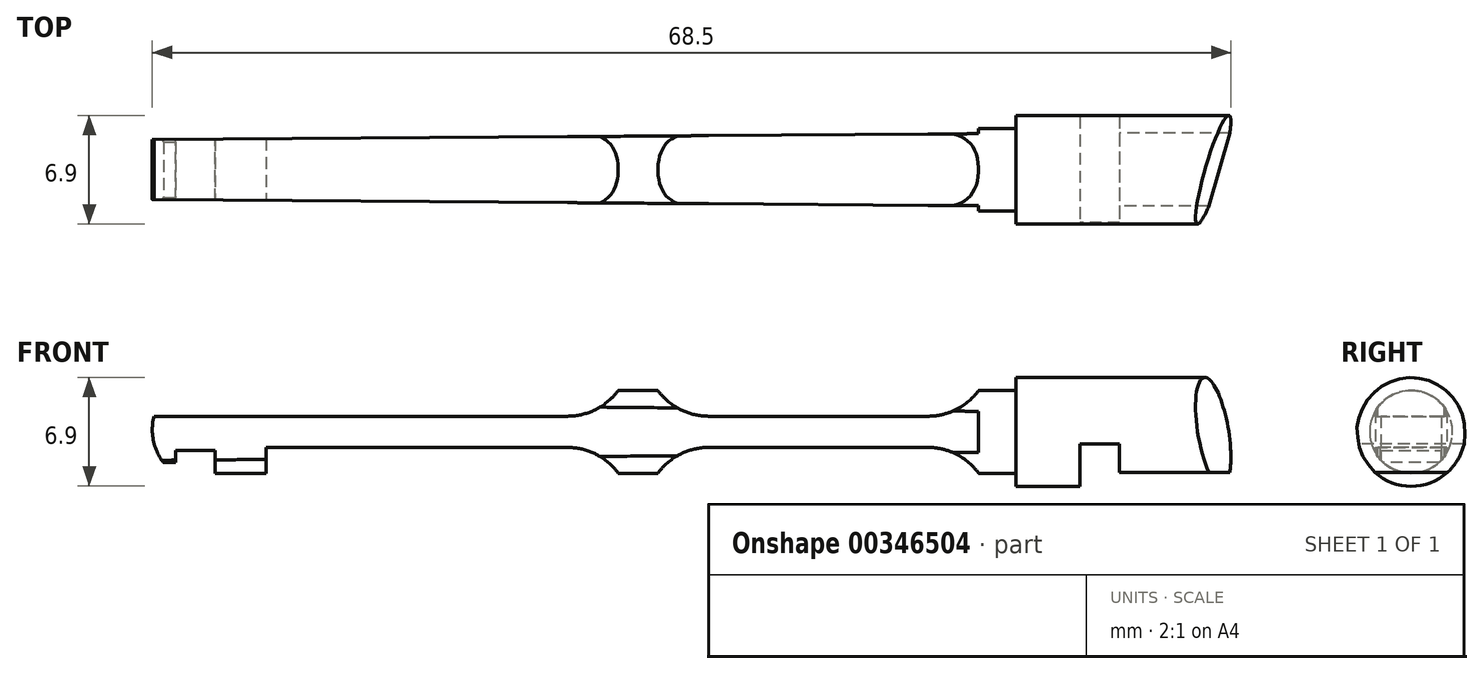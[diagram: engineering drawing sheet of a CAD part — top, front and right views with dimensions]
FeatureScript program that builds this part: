
annotation { "Feature Type Name" : "Feature", "Feature Type Description" : "" }
export const myFeature = defineFeature(function(context is Context, id is Id, definition is map)
    precondition{}
    {
        {
            var Q0;
            Q0=qCreatedBy(makeId("Right.planeOp"),FACE);
            var sketch = newSketch(context, id + "F0", { "sketchPlane" : qUnion([Q0])});
            skCircle(sketch, "E0", {"center": v(0, 0) * mm, "radius": 3.45 * mm});
            skSolve(sketch);
        }
        {
            var Q0;
            Q0 = qSketchRegion(id + "F0", true);
            extrude(context, id + "F1", {"entities" : qUnion([Q0]), "depth" : 4.06 * mm, "offsetDistance" : 25.4 * mm});
        }
        {
            var Q0;
            Q0=makeQuery(id+"F1.opExtrude","CAP_FACE",FACE,{"disambiguationData":[OSD([sQuery(id+"F0.wireOp",EDGE,"E0")])],"isStart":false});
            var sketch = newSketch(context, id + "F2", { "sketchPlane" : qUnion([Q0])});
            skCircle(sketch, "E1.0", {"center": v(0, 0) * mm, "radius": 3.45 * mm});
            skSolve(sketch);
        }
        {
            var Q0;
            Q0 = qSketchRegion(id + "F2", true);
            extrude(context, id + "F3", {"entities" : qUnion([Q0]), "operationType" : NewBodyOperationType.ADD, "depth" : 9.58 * mm, "offsetDistance" : 25.4 * mm});
        }
        {
            var Q0;
            Q0=qCreatedBy(makeId("Front.planeOp"),FACE);
            var sketch = newSketch(context, id + "F4", { "sketchPlane" : qUnion([Q0])});
            skLineSegment(sketch, "E2.bottom", {"start": v(4.06, -0.76) * mm, "end": v(6.58, -0.76) * mm});
            skLineSegment(sketch, "E2.top", {"start": v(4.06, -7.11) * mm, "end": v(6.58, -7.11) * mm});
            skLineSegment(sketch, "E2.left", {"start": v(4.06, -0.76) * mm, "end": v(4.06, -7.11) * mm});
            skLineSegment(sketch, "E2.right", {"start": v(6.58, -0.76) * mm, "end": v(6.58, -7.11) * mm});
            skLineSegment(sketch, "E3.0", {"start": v(13.64, 3.45) * mm, "end": v(13.64, -3.45) * mm, "construction": true});
            skSolve(sketch);
        }
        {
            var Q0;
            Q0 = qSketchRegion(id + "F4", true);
            extrude(context, id + "F5", {"entities" : qUnion([Q0]), "operationType" : NewBodyOperationType.REMOVE, "endBound" : BoundingType.THROUGH_ALL, "oppositeDirection" : true, "depth" : 25.4 * mm, "offsetDistance" : 25.4 * mm, "hasSecondDirection" : true, "secondDirectionBound" : BoundingType.THROUGH_ALL, "secondDirectionOppositeDirection" : false, "secondDirectionDepth" : 25.4 * mm});
        }
        {
            var Q0;
            Q0=qCreatedBy(makeId("Front.planeOp"),FACE);
            var sketch = newSketch(context, id + "F6", { "sketchPlane" : qUnion([Q0])});
            skLineSegment(sketch, "E4.bottom", {"start": v(5.64, -2.57) * mm, "end": v(15.16, -2.57) * mm});
            skLineSegment(sketch, "E4.top", {"start": v(5.64, -4.09) * mm, "end": v(15.16, -4.09) * mm});
            skLineSegment(sketch, "E4.left", {"start": v(5.64, -2.57) * mm, "end": v(5.64, -4.09) * mm});
            skLineSegment(sketch, "E4.right", {"start": v(15.16, -2.57) * mm, "end": v(15.16, -4.09) * mm});
            skLineSegment(sketch, "E5.0", {"start": v(13.64, 3.45) * mm, "end": v(13.64, -3.45) * mm, "construction": true});
            skSolve(sketch);
        }
        {
            var Q0;
            Q0 = qSketchRegion(id + "F6", true);
            extrude(context, id + "F7", {"entities" : qUnion([Q0]), "operationType" : NewBodyOperationType.REMOVE, "endBound" : BoundingType.THROUGH_ALL, "oppositeDirection" : true, "depth" : 25.4 * mm, "offsetDistance" : 25.4 * mm, "hasSecondDirection" : true, "secondDirectionBound" : BoundingType.THROUGH_ALL, "secondDirectionOppositeDirection" : false, "secondDirectionDepth" : 25.4 * mm});
        }
        {
            var Q0;
            Q0=makeQuery(id+"F1.opExtrude","CAP_EDGE",EDGE,{"disambiguationData":[OSD([sQuery(id+"F0.wireOp",EDGE,"E0")])],"isStart":true});
            cPlane(context, id + "F8", {"entities" : qUnion([Q0]), "cplaneType" : CPlaneType.LINE_ANGLE, "offset" : 25.4 * mm, "angle" : 62 * degree, "width" : 152.4 * mm, "height" : 152.4 * mm});
        }
        {
            var Q0;
            Q0=qCreatedBy(id+"F8.planeOp",FACE);
            var sketch = newSketch(context, id + "F9", { "sketchPlane" : qUnion([Q0])});
            skLineSegment(sketch, "E6", {"start": v(13.64, -3.45) * mm, "end": v(11.4, -3.45) * mm});
            skLineSegment(sketch, "E7.0", {"start": v(13.64, 3.45) * mm, "end": v(13.64, -3.45) * mm});
            skLineSegment(sketch, "E8", {"start": v(13.64, 3.45) * mm, "end": v(11.4, -3.45) * mm});
            skSolve(sketch);
        }
        {
            var Q0;
            Q0 = qSketchRegion(id + "F9", true);
            extrude(context, id + "F10", {"entities" : qUnion([Q0]), "operationType" : NewBodyOperationType.REMOVE, "endBound" : BoundingType.THROUGH_ALL, "oppositeDirection" : true, "depth" : 25.4 * mm, "offsetDistance" : 25.4 * mm, "hasSecondDirection" : true, "secondDirectionBound" : BoundingType.THROUGH_ALL, "secondDirectionOppositeDirection" : false, "secondDirectionDepth" : 25.4 * mm});
        }
        {
            var Q0;
            Q0=makeQuery(id+"F1.opExtrude","CAP_FACE",FACE,{"disambiguationData":[OSD([sQuery(id+"F0.wireOp",EDGE,"E0")])],"isStart":true});
            var sketch = newSketch(context, id + "F11", { "sketchPlane" : qUnion([Q0])});
            skCircle(sketch, "E9", {"center": v(0, 0) * mm, "radius": 2.63 * mm});
            skSolve(sketch);
        }
        {
            var Q0;
            Q0 = qSketchRegion(id + "F11", true);
            extrude(context, id + "F12", {"entities" : qUnion([Q0]), "operationType" : NewBodyOperationType.ADD, "depth" : 2.38 * mm, "offsetDistance" : 25.4 * mm});
        }
        {
            var Q0;
            Q0=qCreatedBy(makeId("Top.planeOp"),FACE);
            var sketch = newSketch(context, id + "F13", { "sketchPlane" : qUnion([Q0])});
            skLineSegment(sketch, "E10", {"start": v(-2.38, -2.29) * mm, "end": v(-54.86, -1.9) * mm});
            skLineSegment(sketch, "E11", {"start": v(0, 0) * mm, "end": v(-54.86, 0) * mm, "construction": true});
            skLineSegment(sketch, "E12", {"start": v(-54.86, 0) * mm, "end": v(-54.86, -1.9) * mm});
            skLineSegment(sketch, "E13.0", {"start": v(-2.38, -2.29) * mm, "end": v(-2.38, 0) * mm});
            skPoint(sketch, "E14.orphan", {"position": v(-3.84, -2.28) * mm});
            skPoint(sketch, "E15.orphan", {"position": v(-2.38, -2.63) * mm});
            skPoint(sketch, "E16.orphan", {"position": v(-2.38, 2.63) * mm});
            skLineSegment(sketch, "E17.MirrorCS", {"start": v(-2.38, 2.29) * mm, "end": v(-2.38, 0) * mm});
            skLineSegment(sketch, "E18.MirrorCS", {"start": v(-2.38, 2.29) * mm, "end": v(-54.86, 1.9) * mm});
            skLineSegment(sketch, "E19.MirrorCS", {"start": v(-54.86, 0) * mm, "end": v(-54.86, 1.9) * mm});
            skSolve(sketch);
        }
        {
            var Q0;
            Q0 = qSketchRegion(id + "F13", true);
            extrude(context, id + "F14", {"entities" : qUnion([Q0]), "operationType" : NewBodyOperationType.ADD, "depth" : 1.98 * mm, "offsetDistance" : 25.4 * mm, "symmetric" : true});
        }
        {
            var Q0;
            Q0=qCreatedBy(makeId("Front.planeOp"),FACE);
            var sketch = newSketch(context, id + "F15", { "sketchPlane" : qUnion([Q0])});
            skLineSegment(sketch, "E20.0", {"start": v(-2.38, -1) * mm, "end": v(-5.6, -1) * mm});
            skLineSegment(sketch, "E21.0", {"start": v(-2.38, 1) * mm, "end": v(-5.6, 1) * mm});
            skPoint(sketch, "E22.visualSharp", {"position": v(-2.38, -1) * mm});
            skLineSegment(sketch, "E23.0", {"start": v(-2.38, -2.63) * mm, "end": v(-2.38, -1) * mm});
            skArc(sketch, "E24", {"start": v(-5.6, -1) * mm, "mid": v(-3.79, -1.42) * mm, "end": v(-2.38, -2.63) * mm});
            skPoint(sketch, "E25.orphan", {"position": v(-54.86, -1) * mm});
            skLineSegment(sketch, "E26.trimOffspring", {"start": v(-2.38, 1) * mm, "end": v(-2.38, 2.63) * mm});
            skPoint(sketch, "E27.orphan", {"position": v(-54.86, 1) * mm});
            skArc(sketch, "E28", {"start": v(-5.6, 1) * mm, "mid": v(-3.79, 1.42) * mm, "end": v(-2.38, 2.63) * mm});
            skSolve(sketch);
        }
        {
            var Q0;
            Q0 = qSketchRegion(id + "F15", true);
            var Q1;
            Q1=makeQuery(id+"F14.opExtrude","SWEPT_FACE",FACE,{"disambiguationData":[OSD([sQuery(id+"F13.wireOp",EDGE,"E10")])]});
            var Q2;
            Q2=makeQuery(id+"F14.opExtrude","SWEPT_FACE",FACE,{"disambiguationData":[OSD([sQuery(id+"F13.wireOp",EDGE,"E18.MirrorCS")])]});
            extrude(context, id + "F16", {"entities" : qUnion([Q0]), "operationType" : NewBodyOperationType.ADD, "endBound" : BoundingType.UP_TO_SURFACE, "depth" : 25.4 * mm, "endBoundEntityFace" : qUnion([Q1]), "offsetDistance" : 25.4 * mm, "hasSecondDirection" : true, "secondDirectionBound" : BoundingType.UP_TO_SURFACE, "secondDirectionOppositeDirection" : true, "secondDirectionDepth" : 25.4 * mm, "secondDirectionBoundEntityFace" : qUnion([Q2])});
        }
        {
            var Q0;
            Q0=qCreatedBy(makeId("Front.planeOp"),FACE);
            var sketch = newSketch(context, id + "F17", { "sketchPlane" : qUnion([Q0])});
            skLineSegment(sketch, "E29", {"start": v(0, 0) * mm, "end": v(-24.01, 0) * mm, "construction": true});
            skLineSegment(sketch, "E30.bottom", {"start": v(-23.02, -3.06) * mm, "end": v(-25, -3.06) * mm});
            skLineSegment(sketch, "E30.top", {"start": v(-23.02, 3.06) * mm, "end": v(-25, 3.06) * mm});
            skLineSegment(sketch, "E30.left", {"start": v(-23.02, -3.06) * mm, "end": v(-23.02, 3.06) * mm});
            skLineSegment(sketch, "E30.right", {"start": v(-25, -3.06) * mm, "end": v(-25, 3.06) * mm});
            skPoint(sketch, "E30.middle", {"position": v(-24.01, 0) * mm});
            skLineSegment(sketch, "E31.0", {"start": v(0, 3.45) * mm, "end": v(0, -3.45) * mm, "construction": true});
            skSolve(sketch);
        }
        {
            var Q0;
            Q0 = qSketchRegion(id + "F17", true);
            var Q1;
            Q1=makeQuery(id+"F14.opExtrude","SWEPT_FACE",FACE,{"disambiguationData":[OSD([sQuery(id+"F13.wireOp",EDGE,"E18.MirrorCS")])]});
            var Q2;
            Q2=makeQuery(id+"F14.opExtrude","SWEPT_FACE",FACE,{"disambiguationData":[OSD([sQuery(id+"F13.wireOp",EDGE,"E10")])]});
            extrude(context, id + "F18", {"entities" : qUnion([Q0]), "operationType" : NewBodyOperationType.ADD, "endBound" : BoundingType.UP_TO_SURFACE, "oppositeDirection" : true, "depth" : 25.4 * mm, "endBoundEntityFace" : qUnion([Q1]), "offsetDistance" : 25.4 * mm, "hasSecondDirection" : true, "secondDirectionBound" : BoundingType.UP_TO_SURFACE, "secondDirectionOppositeDirection" : false, "secondDirectionDepth" : 25.4 * mm, "secondDirectionBoundEntityFace" : qUnion([Q2])});
        }
        {
            var Q0;
            Q0=makeQuery(id+"F18.boolean.opBoolean","INTERSECT",EDGE,{"derivedFrom":[makeQuery(id+"F14.opExtrude","CAP_FACE",FACE,{"disambiguationData":[OSD([sQuery(id+"F13.wireOp",EDGE,"E10"),sQuery(id+"F13.wireOp",EDGE,"E12"),sQuery(id+"F13.wireOp",EDGE,"E13.0"),sQuery(id+"F13.wireOp",EDGE,"E17.MirrorCS"),sQuery(id+"F13.wireOp",EDGE,"E18.MirrorCS"),sQuery(id+"F13.wireOp",EDGE,"E19.MirrorCS")])],"isStart":true}),makeQuery(id+"F18.opExtrude","SWEPT_FACE",FACE,{"disambiguationData":[OSD([sQuery(id+"F17.wireOp",EDGE,"E30.left")])]})]});
            var Q1;
            Q1=makeQuery(id+"F18.boolean.opBoolean","INTERSECT",EDGE,{"derivedFrom":[makeQuery(id+"F14.opExtrude","CAP_FACE",FACE,{"disambiguationData":[OSD([sQuery(id+"F13.wireOp",EDGE,"E10"),sQuery(id+"F13.wireOp",EDGE,"E12"),sQuery(id+"F13.wireOp",EDGE,"E13.0"),sQuery(id+"F13.wireOp",EDGE,"E17.MirrorCS"),sQuery(id+"F13.wireOp",EDGE,"E18.MirrorCS"),sQuery(id+"F13.wireOp",EDGE,"E19.MirrorCS")])],"isStart":false}),makeQuery(id+"F18.opExtrude","SWEPT_FACE",FACE,{"disambiguationData":[OSD([sQuery(id+"F17.wireOp",EDGE,"E30.left")])]})]});
            var Q2;
            Q2=makeQuery(id+"F18.boolean.opBoolean","INTERSECT",EDGE,{"derivedFrom":[makeQuery(id+"F14.opExtrude","CAP_FACE",FACE,{"disambiguationData":[OSD([sQuery(id+"F13.wireOp",EDGE,"E10"),sQuery(id+"F13.wireOp",EDGE,"E12"),sQuery(id+"F13.wireOp",EDGE,"E13.0"),sQuery(id+"F13.wireOp",EDGE,"E17.MirrorCS"),sQuery(id+"F13.wireOp",EDGE,"E18.MirrorCS"),sQuery(id+"F13.wireOp",EDGE,"E19.MirrorCS")])],"isStart":true}),makeQuery(id+"F18.opExtrude","SWEPT_FACE",FACE,{"disambiguationData":[OSD([sQuery(id+"F17.wireOp",EDGE,"E30.right")])]})]});
            var Q3;
            Q3=makeQuery(id+"F18.boolean.opBoolean","INTERSECT",EDGE,{"derivedFrom":[makeQuery(id+"F14.opExtrude","CAP_FACE",FACE,{"disambiguationData":[OSD([sQuery(id+"F13.wireOp",EDGE,"E10"),sQuery(id+"F13.wireOp",EDGE,"E12"),sQuery(id+"F13.wireOp",EDGE,"E13.0"),sQuery(id+"F13.wireOp",EDGE,"E17.MirrorCS"),sQuery(id+"F13.wireOp",EDGE,"E18.MirrorCS"),sQuery(id+"F13.wireOp",EDGE,"E19.MirrorCS")])],"isStart":false}),makeQuery(id+"F18.opExtrude","SWEPT_FACE",FACE,{"disambiguationData":[OSD([sQuery(id+"F17.wireOp",EDGE,"E30.right")])]})]});
            fillet(context, id + "F19", {"entities" : qUnion([Q0, Q1, Q2, Q3]), "radius" : 3.96 * mm, "tangentPropagation" : true, "allowEdgeOverflow" : false});
        }
        {
            var Q0;
            Q0=qCreatedBy(makeId("Front.planeOp"),FACE);
            var sketch = newSketch(context, id + "F20", { "sketchPlane" : qUnion([Q0])});
            skLineSegment(sketch, "E32.top", {"start": v(-50.88, -2.67) * mm, "end": v(-47.63, -2.67) * mm});
            skLineSegment(sketch, "E32.left", {"start": v(-50.88, -1) * mm, "end": v(-50.88, -2.67) * mm});
            skLineSegment(sketch, "E32.right", {"start": v(-47.63, -1) * mm, "end": v(-47.63, -2.67) * mm});
            skLineSegment(sketch, "E33.0", {"start": v(-47.63, -1) * mm, "end": v(-50.88, -1) * mm});
            skPoint(sketch, "E34.orphan", {"position": v(-54.86, -1) * mm});
            skLineSegment(sketch, "E35", {"start": v(-54.86, -1) * mm, "end": v(-54.86, -1.96) * mm});
            skLineSegment(sketch, "E36", {"start": v(-54.86, -1.96) * mm, "end": v(-53.4, -1.96) * mm});
            skLineSegment(sketch, "E37", {"start": v(-53.4, -1.96) * mm, "end": v(-53.4, -1) * mm});
            skLineSegment(sketch, "E38.trimOffspring", {"start": v(-53.4, -1) * mm, "end": v(-54.86, -1) * mm});
            skSolve(sketch);
        }
        {
            var Q0;
            Q0 = qSketchRegion(id + "F20", true);
            var Q1;
            {var subQ0=sQuery(id+"F13.wireOp",EDGE,"E18.MirrorCS");Q1=makeQuery(id+"F18.boolean.opBoolean","MERGE",FACE,{"derivedFrom":[makeQuery(id+"F14.opExtrude","SWEPT_FACE",FACE,{"disambiguationData":[OSD([subQ0])]}),makeQuery(id+"F18.opExtrude","CAP_FACE",FACE,{"disambiguationData":[OSD([subQ0])],"isStart":false})]});}
            var Q2;
            {var subQ0=sQuery(id+"F13.wireOp",EDGE,"E10");Q2=makeQuery(id+"F18.boolean.opBoolean","MERGE",FACE,{"derivedFrom":[makeQuery(id+"F14.opExtrude","SWEPT_FACE",FACE,{"disambiguationData":[OSD([subQ0])]}),makeQuery(id+"F18.opExtrude","CAP_FACE",FACE,{"disambiguationData":[OSD([subQ0])],"isStart":false})]});}
            extrude(context, id + "F21", {"entities" : qUnion([Q0]), "operationType" : NewBodyOperationType.ADD, "endBound" : BoundingType.UP_TO_SURFACE, "oppositeDirection" : true, "depth" : 25.4 * mm, "endBoundEntityFace" : qUnion([Q1]), "offsetDistance" : 25.4 * mm, "hasSecondDirection" : true, "secondDirectionBound" : BoundingType.UP_TO_SURFACE, "secondDirectionOppositeDirection" : false, "secondDirectionDepth" : 25.4 * mm, "secondDirectionBoundEntityFace" : qUnion([Q2])});
        }
        {
            var Q0;
            Q0=qCreatedBy(makeId("Front.planeOp"),FACE);
            var sketch = newSketch(context, id + "F22", { "sketchPlane" : qUnion([Q0])});
            skLineSegment(sketch, "E39.bottom", {"start": v(-50.88, -1) * mm, "end": v(-53.4, -1) * mm});
            skLineSegment(sketch, "E39.top", {"start": v(-50.88, -1.2) * mm, "end": v(-53.4, -1.2) * mm});
            skLineSegment(sketch, "E39.left", {"start": v(-50.88, -1.2) * mm, "end": v(-50.88, -1) * mm});
            skLineSegment(sketch, "E39.right", {"start": v(-53.4, -1.2) * mm, "end": v(-53.4, -1) * mm});
            skSolve(sketch);
        }
        {
            var Q0;
            Q0 = qSketchRegion(id + "F22", true);
            var Q1;
            {var subQ0=sQuery(id+"F13.wireOp",EDGE,"E10");Q1=makeQuery(id+"F21.boolean.opBoolean","MERGE",FACE,{"derivedFrom":[makeQuery(id+"F18.boolean.opBoolean","MERGE",FACE,{"derivedFrom":[makeQuery(id+"F14.opExtrude","SWEPT_FACE",FACE,{"disambiguationData":[OSD([subQ0])]}),makeQuery(id+"F18.opExtrude","CAP_FACE",FACE,{"disambiguationData":[OSD([subQ0])],"isStart":false})]}),makeQuery(id+"F21.opExtrude","CAP_FACE",FACE,{"disambiguationData":[OSD([subQ0]),OD(0.0)],"isStart":false}),makeQuery(id+"F21.opExtrude","CAP_FACE",FACE,{"disambiguationData":[OSD([subQ0]),OD(1.0)],"isStart":false})]});}
            var Q2;
            {var subQ0=sQuery(id+"F13.wireOp",EDGE,"E18.MirrorCS");Q2=makeQuery(id+"F21.boolean.opBoolean","MERGE",FACE,{"derivedFrom":[makeQuery(id+"F18.boolean.opBoolean","MERGE",FACE,{"derivedFrom":[makeQuery(id+"F14.opExtrude","SWEPT_FACE",FACE,{"disambiguationData":[OSD([subQ0])]}),makeQuery(id+"F18.opExtrude","CAP_FACE",FACE,{"disambiguationData":[OSD([subQ0])],"isStart":false})]}),makeQuery(id+"F21.opExtrude","CAP_FACE",FACE,{"disambiguationData":[OSD([subQ0]),OD(0.0)],"isStart":false}),makeQuery(id+"F21.opExtrude","CAP_FACE",FACE,{"disambiguationData":[OSD([subQ0]),OD(1.0)],"isStart":false})]});}
            extrude(context, id + "F23", {"entities" : qUnion([Q0]), "operationType" : NewBodyOperationType.ADD, "endBound" : BoundingType.UP_TO_SURFACE, "depth" : 25.4 * mm, "endBoundEntityFace" : qUnion([Q1]), "offsetDistance" : 25.4 * mm, "hasSecondDirection" : true, "secondDirectionBound" : BoundingType.UP_TO_SURFACE, "secondDirectionOppositeDirection" : true, "secondDirectionDepth" : 25.4 * mm, "secondDirectionBoundEntityFace" : qUnion([Q2])});
        }
        {
            var Q0;
            Q0=qCreatedBy(makeId("Front.planeOp"),FACE);
            var sketch = newSketch(context, id + "F24", { "sketchPlane" : qUnion([Q0])});
            skArc(sketch, "E40", {"start": v(-54.76, 1) * mm, "mid": v(-54.8, -0.55) * mm, "end": v(-54.15, -1.96) * mm});
            skLineSegment(sketch, "E41", {"start": v(-54.76, 1) * mm, "end": v(-54.76, 1.4) * mm});
            skLineSegment(sketch, "E42", {"start": v(-54.76, 1.4) * mm, "end": v(-56.4, 1.4) * mm});
            skLineSegment(sketch, "E43", {"start": v(-56.4, 1.4) * mm, "end": v(-56.4, -2.7) * mm});
            skLineSegment(sketch, "E44", {"start": v(-56.4, -2.7) * mm, "end": v(-54.15, -2.7) * mm});
            skLineSegment(sketch, "E45", {"start": v(-54.15, -2.7) * mm, "end": v(-54.15, -1.96) * mm});
            skSolve(sketch);
        }
        {
            var Q0;
            Q0 = qSketchRegion(id + "F24", true);
            extrude(context, id + "F25", {"entities" : qUnion([Q0]), "operationType" : NewBodyOperationType.REMOVE, "endBound" : BoundingType.THROUGH_ALL, "oppositeDirection" : true, "depth" : 25.4 * mm, "offsetDistance" : 25.4 * mm, "hasSecondDirection" : true, "secondDirectionBound" : BoundingType.THROUGH_ALL, "secondDirectionOppositeDirection" : false, "secondDirectionDepth" : 25.4 * mm});
        }
        {
            var Q0;
            {var subQ0=sQuery(id+"F13.wireOp",EDGE,"E10");var subQ2=makeQuery(id+"F16.opExtrude","SWEPT_FACE",FACE,{"disambiguationData":[OSD([sQuery(id+"F15.wireOp",EDGE,"E23.0")])]});Q0=makeQuery(id+"F16.boolean.opBoolean","SPLIT",FACE,{"disambiguationData":[TD([makeQuery(id+"F14.opExtrude","SWEPT_FACE",FACE,{"disambiguationData":[OSD([subQ0])]})])],"derivedFrom":subQ2});}
            var sketch = newSketch(context, id + "F26", { "sketchPlane" : qUnion([Q0])});
            skCircle(sketch, "E46.0", {"center": v(0, 0) * mm, "radius": 2.63 * mm});
            skCircle(sketch, "E47", {"center": v(0, 0) * mm, "radius": 5.23 * mm});
            skSolve(sketch);
        }
        {
            var Q0;
            Q0 = qSketchRegion(id + "F26", true);
            extrude(context, id + "F27", {"entities" : qUnion([Q0]), "operationType" : NewBodyOperationType.REMOVE, "oppositeDirection" : true, "depth" : 73.4 * mm, "offsetDistance" : 25.4 * mm});
        }
    });
